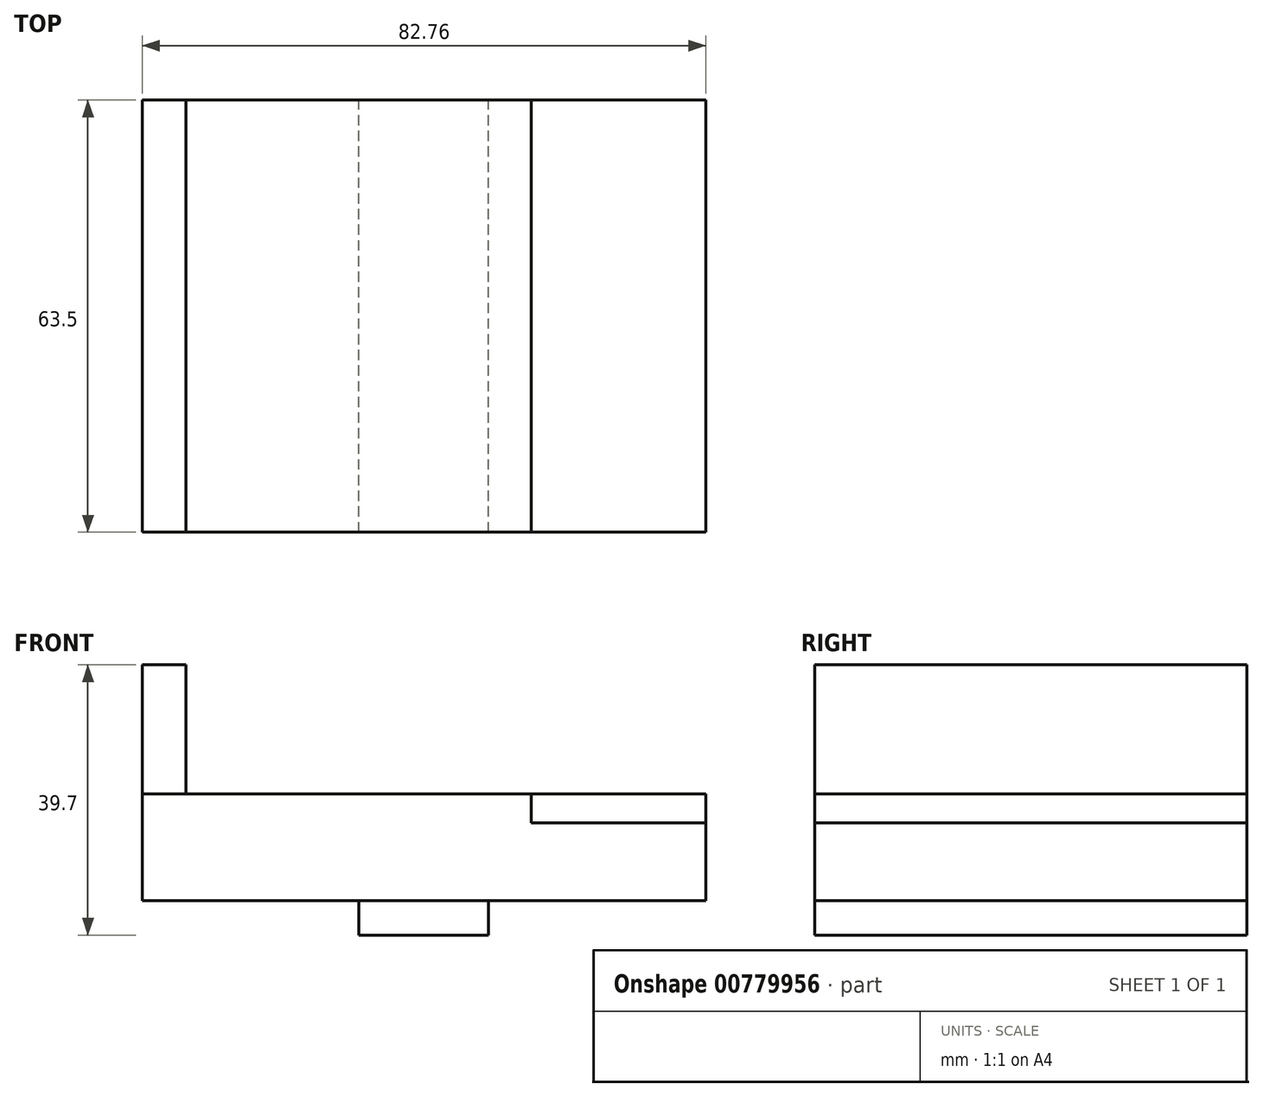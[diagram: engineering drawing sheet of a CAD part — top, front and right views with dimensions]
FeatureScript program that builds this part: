
annotation { "Feature Type Name" : "Feature", "Feature Type Description" : "" }
export const myFeature = defineFeature(function(context is Context, id is Id, definition is map)
    precondition{}
    {
        {
            var Q0;
            Q0=qCreatedBy(makeId("Front.planeOp"),FACE);
            var sketch = newSketch(context, id + "F0", { "sketchPlane" : qUnion([Q0])});
            skLineSegment(sketch, "E0", {"start": v(0, 0) * mm, "end": v(-50.85, 0) * mm});
            skLineSegment(sketch, "E1", {"start": v(0, 0) * mm, "end": v(31.91, 0) * mm});
            skLineSegment(sketch, "E2", {"start": v(-50.85, 0) * mm, "end": v(-19.09, 0) * mm});
            skPoint(sketch, "E3.start.orphan", {"position": v(0, -8.1) * mm});
            skLineSegment(sketch, "E4", {"start": v(-19.09, 0) * mm, "end": v(-19.09, -5.04) * mm});
            skLineSegment(sketch, "E5", {"start": v(-19.09, -5.04) * mm, "end": v(0, -5.04) * mm});
            skLineSegment(sketch, "E6", {"start": v(0, -5.04) * mm, "end": v(0, 0) * mm});
            skLineSegment(sketch, "E7", {"start": v(-50.85, 0) * mm, "end": v(-50.85, 15.73) * mm});
            skLineSegment(sketch, "E8", {"start": v(-50.85, 15.73) * mm, "end": v(6.26, 15.73) * mm});
            skLineSegment(sketch, "E9", {"start": v(6.26, 15.73) * mm, "end": v(6.26, 11.45) * mm});
            skLineSegment(sketch, "E10", {"start": v(6.26, 11.45) * mm, "end": v(31.91, 11.45) * mm});
            skLineSegment(sketch, "E11", {"start": v(31.91, 0) * mm, "end": v(31.91, 11.45) * mm});
            skLineSegment(sketch, "E12", {"start": v(-50.85, 15.73) * mm, "end": v(-50.85, 34.66) * mm});
            skLineSegment(sketch, "E13", {"start": v(-50.85, 34.66) * mm, "end": v(-44.43, 34.66) * mm});
            skLineSegment(sketch, "E14", {"start": v(-44.43, 34.66) * mm, "end": v(-44.43, 15.73) * mm});
            skLineSegment(sketch, "E15", {"start": v(6.26, 15.73) * mm, "end": v(31.91, 15.73) * mm});
            skLineSegment(sketch, "E16", {"start": v(31.91, 11.45) * mm, "end": v(31.91, 15.73) * mm});
            skLineSegment(sketch, "E17", {"start": v(31.91, 15.73) * mm, "end": v(0, 15.73) * mm});
            skLineSegment(sketch, "E18", {"start": v(-44.43, 34.66) * mm, "end": v(0, 34.66) * mm});
            skLineSegment(sketch, "E19", {"start": v(0, 34.66) * mm, "end": v(0, 15.73) * mm});
            skSolve(sketch);
        }
        {
            var Q0;
            Q0=makeQuery(id+"F0.imprint","IMPRINT",FACE,{"disambiguationData":[TD([[makeQuery(id+"F0.imprint","IMPRINT",EDGE,{"derivedFrom":sQuery(id+"F0.wireOp",EDGE,"E0")}),1.0]])]});
            extrude(context, id + "F1", {"entities" : qUnion([Q0]), "depth" : 63.5 * mm, "offsetDistance" : 25.4 * mm});
        }
        {
            var Q0;
            {var subQ0=sQuery(id+"F0.wireOp",EDGE,"E12");Q0=makeQuery(id+"F0.imprint","IMPRINT",FACE,{"disambiguationData":[TD([[makeQuery(id+"F0.imprint","IMPRINT",EDGE,{"derivedFrom":subQ0}),-1.0]])]});}
            extrude(context, id + "F2", {"entities" : qUnion([Q0]), "depth" : 63.5 * mm, "offsetDistance" : 25.4 * mm});
        }
        {
            var Q0;
            Q0=makeQuery(id+"F0.imprint","IMPRINT",FACE,{"disambiguationData":[TD([[makeQuery(id+"F0.imprint","IMPRINT",EDGE,{"derivedFrom":sQuery(id+"F0.wireOp",EDGE,"E0")}),-1.0]])]});
            extrude(context, id + "F3", {"entities" : qUnion([Q0]), "depth" : 63.5 * mm, "offsetDistance" : 25.4 * mm});
        }
        {
            var Q0;
            {var subQ0=sQuery(id+"F0.wireOp",EDGE,"E9");Q0=makeQuery(id+"F0.imprint","IMPRINT",FACE,{"disambiguationData":[TD([[makeQuery(id+"F0.imprint","IMPRINT",EDGE,{"derivedFrom":subQ0}),1.0]])]});}
            extrude(context, id + "F4", {"entities" : qUnion([Q0]), "depth" : 63.5 * mm, "offsetDistance" : 25.4 * mm});
        }
    });
